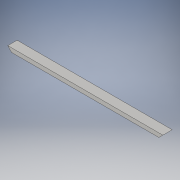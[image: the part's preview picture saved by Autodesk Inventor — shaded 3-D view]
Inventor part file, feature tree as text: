
AUTODESK INVENTOR PART (.ipt)
format: ipt  version: 2016 (Build 200138000, 138)  size: 91,136 bytes
history: native  units: in
note: dims shown in document units (in); Inventor stores cm internally (conversion verified against a paired STEP export)
features: extrude x1, sketch x1
ambient origin geometry x8: Origin, YZ Plane, XZ Plane, XY Plane, X Axis, Y Axis, Z Axis, Center Point
bodies: Solid1 (feature_tree)
feature tree (2):
  extrude  "Extrusion1"  TaperAngle=45.0deg  [1 undecoded]
  sketch  "Sketch1"  dims[d2=45.0deg d3=45.0deg d4=1.5in d6=3.5in d7=0.0in]
note: 1 required parameter value undecoded (feature->parameter linkage not recoverable at this tier; creation-order binding heuristic only, values carry confidence <= 0.55)
